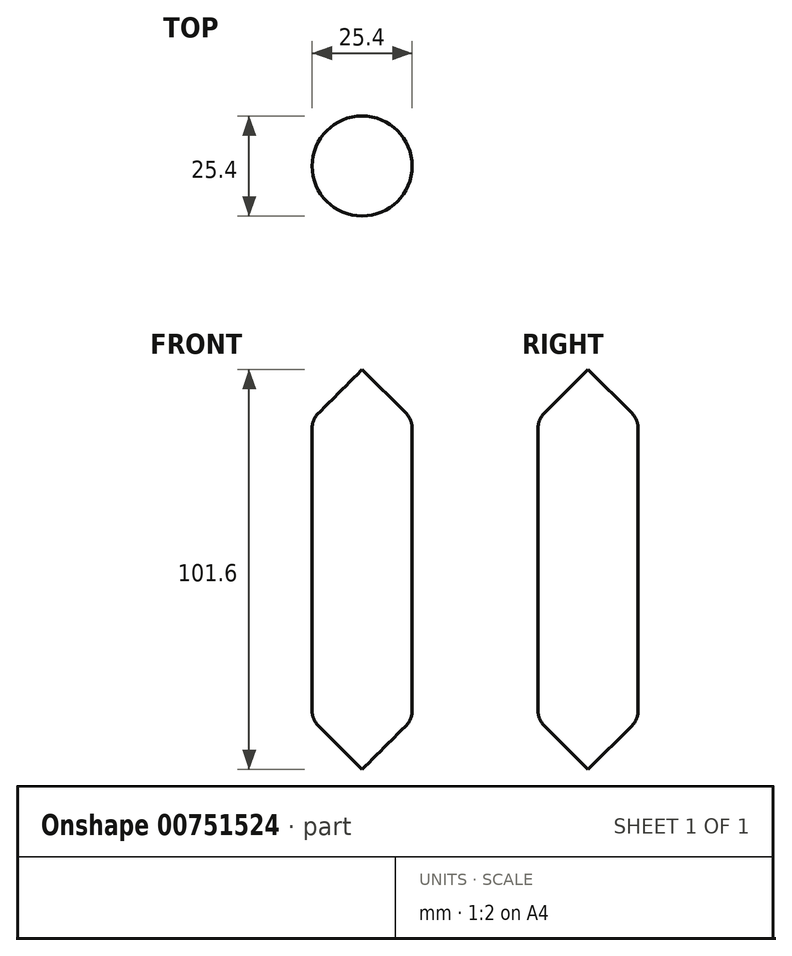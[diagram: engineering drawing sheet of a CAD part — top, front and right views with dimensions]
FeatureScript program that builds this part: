
annotation { "Feature Type Name" : "Feature", "Feature Type Description" : "" }
export const myFeature = defineFeature(function(context is Context, id is Id, definition is map)
    precondition{}
    {
        {
            var Q0;
            Q0=qCreatedBy(makeId("Front.planeOp"),FACE);
            var sketch = newSketch(context, id + "F0", { "sketchPlane" : qUnion([Q0])});
            skLineSegment(sketch, "E0", {"start": v(0, 46.19) * mm, "end": v(0, -43.58) * mm, "construction": true});
            skLineSegment(sketch, "E1", {"start": v(0, 32.1) * mm, "end": v(-12.7, 19.4) * mm});
            skLineSegment(sketch, "E2", {"start": v(-12.7, 19.4) * mm, "end": v(-12.7, -56.8) * mm});
            skLineSegment(sketch, "E3", {"start": v(-12.7, -56.8) * mm, "end": v(0, -69.5) * mm});
            skLineSegment(sketch, "E4", {"start": v(0, -69.5) * mm, "end": v(0, 32.1) * mm});
            skSolve(sketch);
        }
        {
            var Q0;
            Q0 = qSketchRegion(id + "F0", true);
            var Q1;
            Q1=sQuery(id+"F0.wireOp",EDGE,"E0");
            revolve(context, id + "F1", {"surfaceOperationType" : NewSurfaceOperationType.NEW, "entities" : qUnion([Q0]), "axis" : qUnion([Q1]), "revolveType" : RevolveType.FULL});
        }
        {
            var Q0;
            Q0=makeQuery(id+"F1.opRevolve","SWEPT_EDGE",EDGE,{"disambiguationData":[OSD([sQuery(id+"F0.wireOp",EDGE,"E1"),sQuery(id+"F0.wireOp",EDGE,"E2")])]});
            var Q1;
            Q1=makeQuery(id+"F1.opRevolve","SWEPT_EDGE",EDGE,{"disambiguationData":[OSD([sQuery(id+"F0.wireOp",EDGE,"E2"),sQuery(id+"F0.wireOp",EDGE,"E3")])]});
            fillet(context, id + "F2", {"entities" : qUnion([Q0, Q1]), "radius" : 5.08 * mm, "tangentPropagation" : true, "allowEdgeOverflow" : false});
        }
    });
